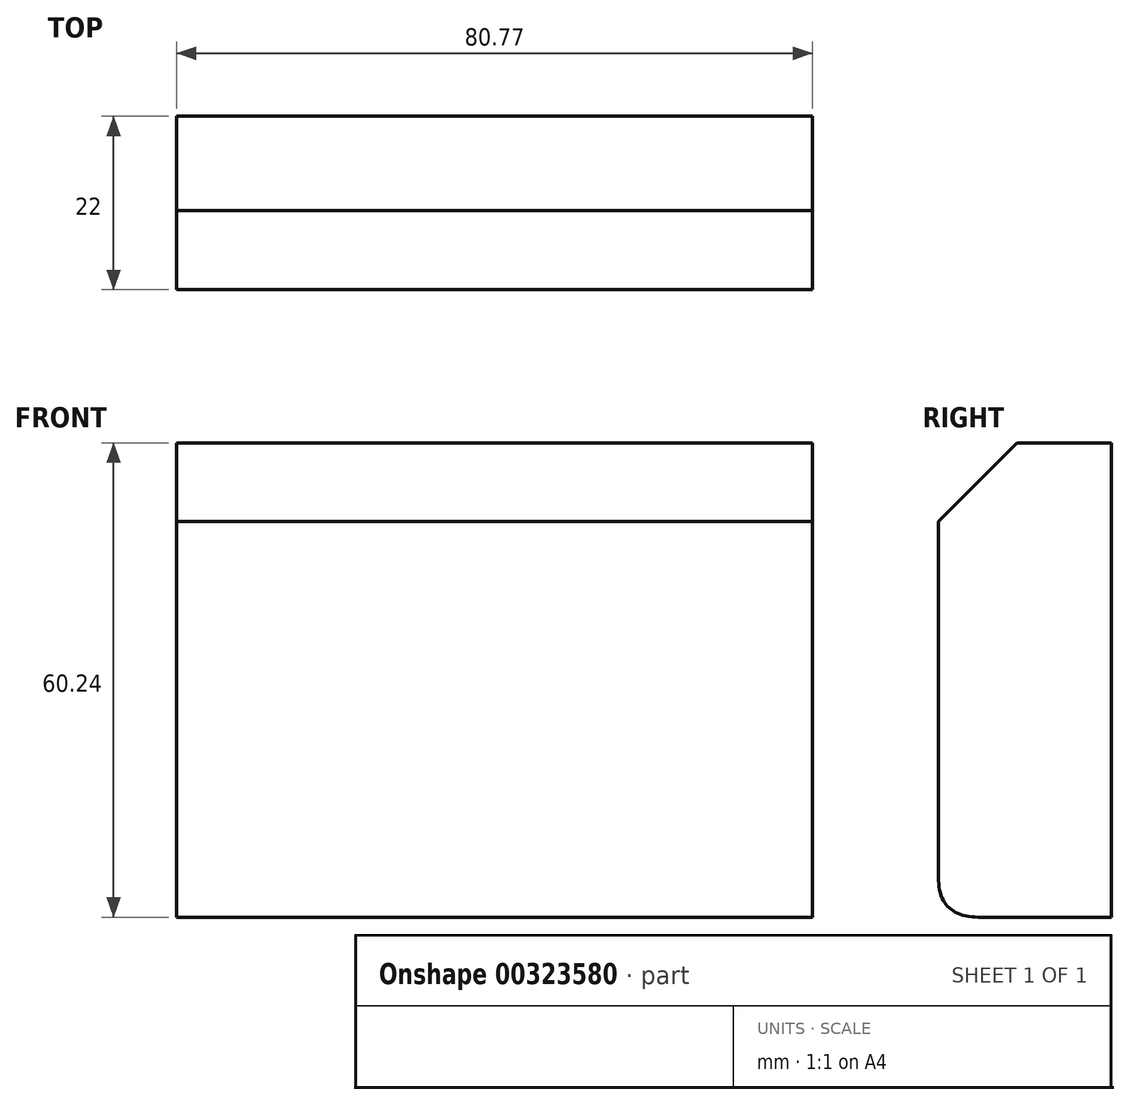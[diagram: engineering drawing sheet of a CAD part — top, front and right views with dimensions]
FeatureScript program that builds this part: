
annotation { "Feature Type Name" : "Feature", "Feature Type Description" : "" }
export const myFeature = defineFeature(function(context is Context, id is Id, definition is map)
    precondition{}
    {
        {
            var Q0;
            Q0=qCreatedBy(makeId("Front.planeOp"),FACE);
            var sketch = newSketch(context, id + "F0", { "sketchPlane" : qUnion([Q0])});
            skLineSegment(sketch, "E0.bottom", {"start": v(41.13, 0) * mm, "end": v(-39.64, 0) * mm});
            skLineSegment(sketch, "E0.top", {"start": v(41.13, -60.24) * mm, "end": v(-39.64, -60.24) * mm});
            skLineSegment(sketch, "E0.left", {"start": v(41.13, 0) * mm, "end": v(41.13, -60.24) * mm});
            skLineSegment(sketch, "E0.right", {"start": v(-39.64, 0) * mm, "end": v(-39.64, -60.24) * mm});
            skLineSegment(sketch, "E1.bottom", {"start": v(41.13, 83.67) * mm, "end": v(-39.64, 83.67) * mm, "construction": true});
            skLineSegment(sketch, "E1.top", {"start": v(41.13, 0) * mm, "end": v(-39.64, 0) * mm, "construction": true});
            skLineSegment(sketch, "E1.left", {"start": v(41.13, 83.67) * mm, "end": v(41.13, 0) * mm, "construction": true});
            skLineSegment(sketch, "E1.right", {"start": v(-39.64, 83.67) * mm, "end": v(-39.64, 0) * mm, "construction": true});
            skSolve(sketch);
        }
        {
            var Q0;
            Q0 = qSketchRegion(id + "F0", true);
            extrude(context, id + "F1", {"entities" : qUnion([Q0]), "depth" : 22 * mm});
        }
        {
            var Q0;
            Q0=makeQuery(id+"F1.opExtrude","CAP_EDGE",EDGE,{"disambiguationData":[OSD([sQuery(id+"F0.wireOp",EDGE,"E0.top")])],"isStart":false});
            fillet(context, id + "F2", {"entities" : qUnion([Q0]), "radius" : 5.08 * mm, "tangentPropagation" : true, "rho" : 0.5, "crossSection" : FilletCrossSection.CONIC, "allowEdgeOverflow" : false});
        }
        {
            var Q0;
            Q0=makeQuery(id+"F1.opExtrude","CAP_EDGE",EDGE,{"disambiguationData":[OSD([sQuery(id+"F0.wireOp",EDGE,"E0.bottom")])],"isStart":false});
            chamfer(context, id + "F3", {"entities" : qUnion([Q0]), "width" : 10 * mm, "tangentPropagation" : true});
        }
    });
